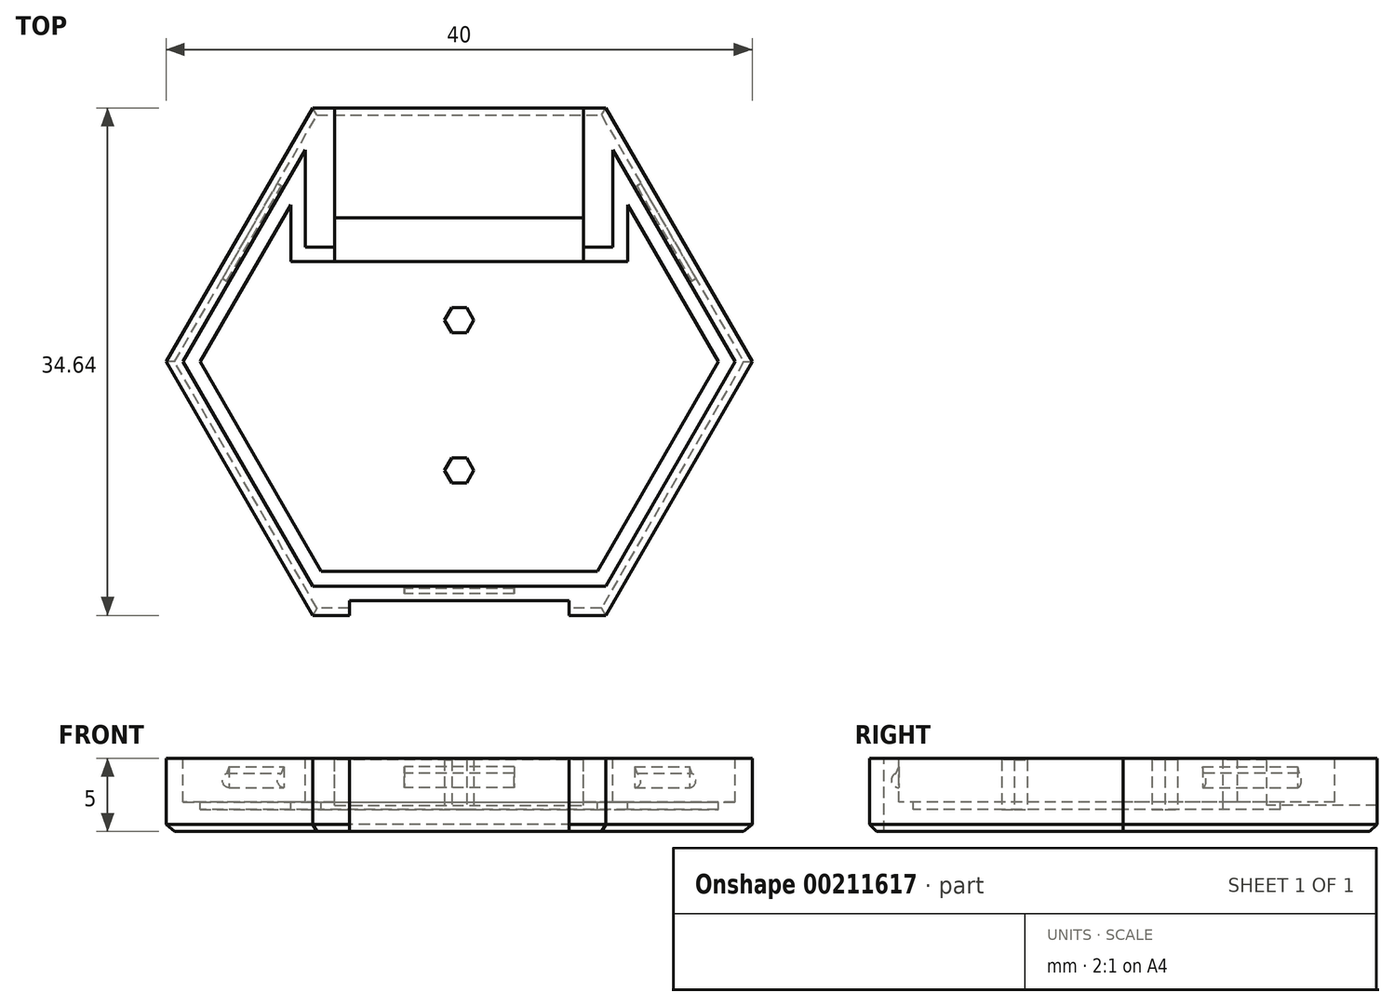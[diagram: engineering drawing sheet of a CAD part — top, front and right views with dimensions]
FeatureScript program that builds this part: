
annotation { "Feature Type Name" : "Feature", "Feature Type Description" : "" }
export const myFeature = defineFeature(function(context is Context, id is Id, definition is map)
    precondition{}
    {
        {
            var Q0;
            Q0=qCreatedBy(makeId("Top.planeOp"),FACE);
            var sketch = newSketch(context, id + "F0", { "sketchPlane" : qUnion([Q0])});
            skCircle(sketch, "E0.cCircle", {"center": v(0, 0) * mm, "radius": 20 * mm, "construction": true});
            skLineSegment(sketch, "E0.0", {"start": v(10, 17.32) * mm, "end": v(20, 0) * mm});
            skLineSegment(sketch, "E0.1", {"start": v(20, 0) * mm, "end": v(10, -17.32) * mm});
            skLineSegment(sketch, "E0.2", {"start": v(10, -17.32) * mm, "end": v(-10, -17.32) * mm});
            skLineSegment(sketch, "E0.3", {"start": v(-10, -17.32) * mm, "end": v(-20, 0) * mm});
            skLineSegment(sketch, "E0.4", {"start": v(-20, 0) * mm, "end": v(-10, 17.32) * mm});
            skLineSegment(sketch, "E0.5", {"start": v(-10, 17.32) * mm, "end": v(10, 17.32) * mm});
            skSolve(sketch);
        }
        {
            var Q0;
            Q0 = qSketchRegion(id + "F0", true);
            extrude(context, id + "F1", {"entities" : qUnion([Q0]), "depth" : 5 * mm});
        }
        {
            var Q0;
            Q0=makeQuery(id+"F1.opExtrude","SWEPT_FACE",FACE,{"disambiguationData":[OSD([sQuery(id+"F0.wireOp",EDGE,"E0.2")])]});
            var sketch = newSketch(context, id + "F2", { "sketchPlane" : qUnion([Q0])});
            skLineSegment(sketch, "E1.bottom", {"start": v(-7.5, 0) * mm, "end": v(7.5, 0) * mm});
            skLineSegment(sketch, "E1.top", {"start": v(-7.5, 5) * mm, "end": v(7.5, 5) * mm});
            skLineSegment(sketch, "E1.left", {"start": v(-7.5, 0) * mm, "end": v(-7.5, 5) * mm});
            skLineSegment(sketch, "E1.right", {"start": v(7.5, 0) * mm, "end": v(7.5, 5) * mm});
            skPoint(sketch, "E1.middle", {"position": v(0, 2.5) * mm});
            skLineSegment(sketch, "E2", {"start": v(-7.5, 5) * mm, "end": v(-7.5, 3.33) * mm});
            skLineSegment(sketch, "E3", {"start": v(-7.5, 3.33) * mm, "end": v(7.5, 3.33) * mm});
            skLineSegment(sketch, "E4", {"start": v(7.5, 3.33) * mm, "end": v(7.5, 1.67) * mm});
            skLineSegment(sketch, "E5", {"start": v(7.5, 1.67) * mm, "end": v(-7.5, 1.67) * mm});
            skLineSegment(sketch, "E6", {"start": v(-7.5, 1.67) * mm, "end": v(-7.5, 0) * mm});
            skLineSegment(sketch, "E7.left", {"start": v(-7.5, 5) * mm, "end": v(-7.5, 5) * mm});
            skLineSegment(sketch, "E7.right", {"start": v(7.5, 5) * mm, "end": v(7.5, 5) * mm});
            skSolve(sketch);
        }
        {
            var Q0;
            Q0=makeQuery(id+"F2.imprint","IMPRINT",FACE,{"disambiguationData":[TD([[makeQuery(id+"F2.imprint","IMPRINT",EDGE,{"derivedFrom":sQuery(id+"F2.wireOp",EDGE,"E1.left")}),-1.0]])]});
            var Q1;
            Q1=makeQuery(id+"F2.imprint","IMPRINT",FACE,{"disambiguationData":[TD([[makeQuery(id+"F2.imprint","IMPRINT",EDGE,{"derivedFrom":sQuery(id+"F2.wireOp",EDGE,"E1.top")}),1.0]])]});
            extrude(context, id + "F3", {"entities" : qUnion([Q0, Q1]), "operationType" : NewBodyOperationType.REMOVE, "oppositeDirection" : true, "depth" : 1 * mm});
        }
        {
            var Q0;
            Q0=makeQuery(id+"F1.opExtrude","CAP_FACE",FACE,{"disambiguationData":[OSD([sQuery(id+"F0.wireOp",EDGE,"E0.0"),sQuery(id+"F0.wireOp",EDGE,"E0.1"),sQuery(id+"F0.wireOp",EDGE,"E0.2"),sQuery(id+"F0.wireOp",EDGE,"E0.3"),sQuery(id+"F0.wireOp",EDGE,"E0.4"),sQuery(id+"F0.wireOp",EDGE,"E0.5")])],"isStart":false});
            var sketch = newSketch(context, id + "F4", { "sketchPlane" : qUnion([Q0])});
            skLineSegment(sketch, "E8.0", {"start": v(-18.85, 0) * mm, "end": v(-10, -15.32) * mm});
            skLineSegment(sketch, "E8.1", {"start": v(10, -15.32) * mm, "end": v(18.85, 0) * mm});
            skLineSegment(sketch, "E8.2", {"start": v(18.85, 0) * mm, "end": v(9.42, 16.32) * mm});
            skLineSegment(sketch, "E8.3", {"start": v(-10, -15.32) * mm, "end": v(10, -15.32) * mm});
            skLineSegment(sketch, "E8.4", {"start": v(9.42, 16.32) * mm, "end": v(-9.42, 16.32) * mm});
            skLineSegment(sketch, "E8.5", {"start": v(-9.42, 16.32) * mm, "end": v(-18.85, 0) * mm});
            skLineSegment(sketch, "E9.0", {"start": v(8.85, 15.32) * mm, "end": v(-8.85, 15.32) * mm});
            skLineSegment(sketch, "E9.1", {"start": v(-17.7, 0) * mm, "end": v(-9.42, -14.32) * mm});
            skLineSegment(sketch, "E9.2", {"start": v(-9.42, -14.32) * mm, "end": v(9.42, -14.32) * mm});
            skLineSegment(sketch, "E9.3", {"start": v(-8.85, 15.32) * mm, "end": v(-17.7, 0) * mm});
            skLineSegment(sketch, "E9.4", {"start": v(9.42, -14.32) * mm, "end": v(17.7, 0) * mm});
            skLineSegment(sketch, "E9.5", {"start": v(17.7, 0) * mm, "end": v(8.85, 15.32) * mm});
            skLineSegment(sketch, "E10.bottom", {"start": v(8.5, 17.32) * mm, "end": v(-8.5, 17.32) * mm});
            skLineSegment(sketch, "E10.top", {"start": v(8.5, 9.82) * mm, "end": v(-8.5, 9.82) * mm});
            skLineSegment(sketch, "E10.left", {"start": v(8.5, 17.32) * mm, "end": v(8.5, 9.82) * mm});
            skLineSegment(sketch, "E10.right", {"start": v(-8.5, 17.32) * mm, "end": v(-8.5, 9.82) * mm});
            skPoint(sketch, "E10.middle", {"position": v(0, 13.57) * mm});
            skLineSegment(sketch, "E11.0", {"start": v(10.5, 17.32) * mm, "end": v(10.5, 7.82) * mm});
            skLineSegment(sketch, "E11.1", {"start": v(10.5, 7.82) * mm, "end": v(-10.5, 7.82) * mm});
            skLineSegment(sketch, "E11.2", {"start": v(-10.5, 17.32) * mm, "end": v(-10.5, 7.82) * mm});
            skLineSegment(sketch, "E12.0", {"start": v(11.5, 17.32) * mm, "end": v(11.5, 6.82) * mm});
            skLineSegment(sketch, "E12.1", {"start": v(11.5, 6.82) * mm, "end": v(-11.5, 6.82) * mm});
            skLineSegment(sketch, "E12.2", {"start": v(-11.5, 17.32) * mm, "end": v(-11.5, 6.82) * mm});
            skPoint(sketch, "E13", {"position": v(-11.5, 10.72) * mm});
            skPoint(sketch, "E14", {"position": v(-11.5, 12.72) * mm});
            skPoint(sketch, "E15", {"position": v(-10.5, 14.45) * mm});
            skPoint(sketch, "E16", {"position": v(-10.5, 12.45) * mm});
            skPoint(sketch, "E17", {"position": v(10.5, 12.45) * mm});
            skPoint(sketch, "E18", {"position": v(11.5, 12.72) * mm});
            skPoint(sketch, "E19", {"position": v(10.5, 14.45) * mm});
            skPoint(sketch, "E20", {"position": v(11.5, 10.72) * mm});
            skLineSegment(sketch, "E21", {"start": v(-8.5, 9.82) * mm, "end": v(-8.5, 6.82) * mm});
            skLineSegment(sketch, "E22", {"start": v(8.5, 9.82) * mm, "end": v(8.5, 6.82) * mm});
            skSolve(sketch);
        }
        {
            var Q0;
            {var subQ5=sQuery(id+"F4.wireOp",EDGE,"E10.top");Q0=makeQuery(id+"F4.imprint","IMPRINT",FACE,{"disambiguationData":[TD([[makeQuery(id+"F4.imprint","IMPRINT",EDGE,{"derivedFrom":subQ5}),-1.0]])]});}
            var Q1;
            {var subQ0=sQuery(id+"F4.wireOp",EDGE,"E10.left");var subQ1=sQuery(id+"F4.wireOp",EDGE,"E8.4");var subQ2=makeQuery(id+"F4.imprint","INTERSECT",VERTEX,{"derivedFrom":[subQ1,subQ0]});Q1=makeQuery(id+"F4.imprint","IMPRINT",FACE,{"disambiguationData":[TD([[makeQuery(id+"F4.imprint","IMPRINT",EDGE,{"disambiguationData":[TD([[subQ2,-1.0]])],"derivedFrom":subQ1}),1.0]])]});}
            var Q2;
            {var subQ5=sQuery(id+"F4.wireOp",EDGE,"E10.bottom");Q2=makeQuery(id+"F4.imprint","IMPRINT",FACE,{"disambiguationData":[TD([[makeQuery(id+"F4.imprint","IMPRINT",EDGE,{"derivedFrom":subQ5}),-1.0]])]});}
            extrude(context, id + "F5", {"entities" : qUnion([Q0, Q1, Q2]), "operationType" : NewBodyOperationType.REMOVE, "oppositeDirection" : true, "depth" : 3.2 * mm});
        }
        {
            var Q0;
            {var subQ1=sQuery(id+"F4.wireOp",EDGE,"E9.1");Q0=makeQuery(id+"F4.imprint","IMPRINT",FACE,{"disambiguationData":[TD([[makeQuery(id+"F4.imprint","IMPRINT",EDGE,{"derivedFrom":subQ1}),1.0]])]});}
            extrude(context, id + "F6", {"entities" : qUnion([Q0]), "operationType" : NewBodyOperationType.REMOVE, "oppositeDirection" : true, "depth" : 3.5 * mm});
        }
        {
            var Q0;
            {var subQ0=sQuery(id+"F4.wireOp",EDGE,"E10.top");Q0=makeQuery(id+"F4.imprint","IMPRINT",FACE,{"disambiguationData":[TD([[makeQuery(id+"F4.imprint","IMPRINT",EDGE,{"derivedFrom":subQ0}),1.0]])]});}
            var Q1;
            {var subQ0=sQuery(id+"F4.wireOp",EDGE,"E22");var subQ1=sQuery(id+"F4.wireOp",EDGE,"E11.1");var subQ2=makeQuery(id+"F4.imprint","INTERSECT",VERTEX,{"derivedFrom":[subQ1,subQ0]});Q1=makeQuery(id+"F4.imprint","IMPRINT",FACE,{"disambiguationData":[TD([[makeQuery(id+"F4.imprint","IMPRINT",EDGE,{"disambiguationData":[TD([[subQ2,-1.0]])],"derivedFrom":subQ1}),1.0]])]});}
            extrude(context, id + "F7", {"entities" : qUnion([Q0, Q1]), "operationType" : NewBodyOperationType.REMOVE, "oppositeDirection" : true, "depth" : 0.1 * mm});
        }
        {
            var Q0;
            {var subQ5=sQuery(id+"F4.wireOp",EDGE,"E11.2");var subQ8=sQuery(id+"F4.wireOp",EDGE,"E9.3");var subQ9=makeQuery(id+"F4.imprint","INTERSECT",VERTEX,{"derivedFrom":[subQ8,subQ5]});Q0=makeQuery(id+"F4.imprint","IMPRINT",FACE,{"disambiguationData":[TD([[makeQuery(id+"F4.imprint","IMPRINT",EDGE,{"disambiguationData":[TD([[subQ9,-1.0]])],"derivedFrom":subQ8}),1.0]])]});}
            var Q1;
            {var subQ0=sQuery(id+"F4.wireOp",EDGE,"E11.2");var subQ1=sQuery(id+"F4.wireOp",EDGE,"E8.5");var subQ2=makeQuery(id+"F4.imprint","INTERSECT",VERTEX,{"derivedFrom":[subQ1,subQ0]});Q1=makeQuery(id+"F4.imprint","IMPRINT",FACE,{"disambiguationData":[TD([[makeQuery(id+"F4.imprint","IMPRINT",EDGE,{"disambiguationData":[TD([[subQ2,-1.0]])],"derivedFrom":subQ1}),1.0]])]});}
            var Q2;
            {var subQ5=sQuery(id+"F4.wireOp",EDGE,"E8.0");Q2=makeQuery(id+"F4.imprint","IMPRINT",FACE,{"disambiguationData":[TD([[makeQuery(id+"F4.imprint","IMPRINT",EDGE,{"derivedFrom":subQ5}),1.0]])]});}
            var Q3;
            {var subQ1=sQuery(id+"F4.wireOp",EDGE,"E12.0");var subQ3=sQuery(id+"F4.wireOp",EDGE,"E9.5");var subQ4=makeQuery(id+"F4.imprint","INTERSECT",VERTEX,{"derivedFrom":[subQ3,subQ1]});Q3=makeQuery(id+"F4.imprint","IMPRINT",FACE,{"disambiguationData":[TD([[makeQuery(id+"F4.imprint","IMPRINT",EDGE,{"disambiguationData":[TD([[subQ4,-1.0]])],"derivedFrom":subQ3}),1.0]])]});}
            var Q4;
            {var subQ0=sQuery(id+"F4.wireOp",EDGE,"E12.0");var subQ1=sQuery(id+"F4.wireOp",EDGE,"E8.2");var subQ2=makeQuery(id+"F4.imprint","INTERSECT",VERTEX,{"derivedFrom":[subQ1,subQ0]});Q4=makeQuery(id+"F4.imprint","IMPRINT",FACE,{"disambiguationData":[TD([[makeQuery(id+"F4.imprint","IMPRINT",EDGE,{"disambiguationData":[TD([[subQ2,-1.0]])],"derivedFrom":subQ1}),1.0]])]});}
            extrude(context, id + "F8", {"entities" : qUnion([Q0, Q1, Q2, Q3, Q4]), "operationType" : NewBodyOperationType.REMOVE, "oppositeDirection" : true, "depth" : 3 * mm});
        }
        {
            var Q0;
            Q0=makeQuery(id+"F6.boolean.opBoolean","COPY",FACE,{"derivedFrom":makeQuery(id+"F6.opExtrude","CAP_FACE",FACE,{"disambiguationData":[OSD([sQuery(id+"F4.wireOp",EDGE,"E9.1"),sQuery(id+"F4.wireOp",EDGE,"E9.2"),sQuery(id+"F4.wireOp",EDGE,"E9.3"),sQuery(id+"F4.wireOp",EDGE,"E9.4"),sQuery(id+"F4.wireOp",EDGE,"E9.5"),sQuery(id+"F4.wireOp",EDGE,"E12.0"),sQuery(id+"F4.wireOp",EDGE,"E12.1"),sQuery(id+"F4.wireOp",EDGE,"E12.2")])],"isStart":false})});
            var sketch = newSketch(context, id + "F9", { "sketchPlane" : qUnion([Q0])});
            skCircle(sketch, "E23.cCircle", {"center": v(0, 2.84) * mm, "radius": 1 * mm, "construction": true});
            skLineSegment(sketch, "E23.0", {"start": v(0.5, 1.97) * mm, "end": v(-0.5, 1.97) * mm});
            skLineSegment(sketch, "E23.1", {"start": v(-0.5, 1.97) * mm, "end": v(-1, 2.84) * mm});
            skLineSegment(sketch, "E23.2", {"start": v(-1, 2.84) * mm, "end": v(-0.5, 3.7) * mm});
            skLineSegment(sketch, "E23.3", {"start": v(-0.5, 3.7) * mm, "end": v(0.5, 3.7) * mm});
            skLineSegment(sketch, "E23.4", {"start": v(0.5, 3.7) * mm, "end": v(1, 2.84) * mm});
            skLineSegment(sketch, "E23.5", {"start": v(1, 2.84) * mm, "end": v(0.5, 1.97) * mm});
            skLineSegment(sketch, "E24", {"start": v(-6.8, -2.3) * mm, "end": v(7.3, -2.3) * mm});
            skLineSegment(sketch, "E25.MirrorCS", {"start": v(0.5, -6.56) * mm, "end": v(-0.5, -6.56) * mm});
            skLineSegment(sketch, "E26.MirrorCS", {"start": v(-0.5, -6.56) * mm, "end": v(-1, -7.43) * mm});
            skLineSegment(sketch, "E27.MirrorCS", {"start": v(-1, -7.43) * mm, "end": v(-0.5, -8.3) * mm});
            skLineSegment(sketch, "E28.MirrorCS", {"start": v(-0.5, -8.3) * mm, "end": v(0.5, -8.3) * mm});
            skLineSegment(sketch, "E29.MirrorCS", {"start": v(0.5, -8.3) * mm, "end": v(1, -7.43) * mm});
            skCircle(sketch, "E30.MirrorC", {"center": v(0, -7.43) * mm, "radius": 1 * mm, "construction": true});
            skLineSegment(sketch, "E31.MirrorCS", {"start": v(1, -7.43) * mm, "end": v(0.5, -6.56) * mm});
            skSolve(sketch);
        }
        {
            var Q0;
            Q0=makeQuery(id+"F9.imprint","IMPRINT",FACE,{"disambiguationData":[TD([[makeQuery(id+"F9.imprint","IMPRINT",EDGE,{"derivedFrom":sQuery(id+"F9.wireOp",EDGE,"E23.0")}),-1.0]])]});
            var Q1;
            Q1=makeQuery(id+"F9.imprint","IMPRINT",FACE,{"disambiguationData":[TD([[makeQuery(id+"F9.imprint","IMPRINT",EDGE,{"derivedFrom":sQuery(id+"F9.wireOp",EDGE,"E25.MirrorCS")}),1.0]])]});
            extrude(context, id + "F10", {"entities" : qUnion([Q0, Q1]), "operationType" : NewBodyOperationType.ADD, "depth" : 3.4 * mm});
        }
        {
            var Q0;
            Q0=makeQuery(id+"F8.boolean.opBoolean","COPY",FACE,{"derivedFrom":makeQuery(id+"F8.opExtrude","SWEPT_FACE",FACE,{"disambiguationData":[OSD([sQuery(id+"F4.wireOp",EDGE,"E8.3")])]})});
            var sketch = newSketch(context, id + "F11", { "sketchPlane" : qUnion([Q0])});
            skLineSegment(sketch, "E32.bottom", {"start": v(3.75, 4) * mm, "end": v(-3.75, 4) * mm});
            skLineSegment(sketch, "E32.top", {"start": v(3.75, 3) * mm, "end": v(-3.75, 3) * mm});
            skLineSegment(sketch, "E32.left", {"start": v(3.75, 4) * mm, "end": v(3.75, 3) * mm});
            skLineSegment(sketch, "E32.right", {"start": v(-3.75, 4) * mm, "end": v(-3.75, 3) * mm});
            skPoint(sketch, "E32.middle", {"position": v(0, 3.5) * mm});
            skLineSegment(sketch, "E33", {"start": v(-3.75, 3.5) * mm, "end": v(3.75, 3.5) * mm});
            skSolve(sketch);
        }
        {
            var Q0;
            Q0=makeQuery(id+"F8.boolean.opBoolean","COPY",FACE,{"derivedFrom":makeQuery(id+"F8.opExtrude","SWEPT_FACE",FACE,{"disambiguationData":[OSD([sQuery(id+"F4.wireOp",EDGE,"E8.2")])]})});
            var sketch = newSketch(context, id + "F12", { "sketchPlane" : qUnion([Q0])});
            skLineSegment(sketch, "E34.bottom", {"start": v(3.17, 4) * mm, "end": v(-4.33, 4) * mm});
            skLineSegment(sketch, "E34.top", {"start": v(3.17, 3) * mm, "end": v(-4.33, 3) * mm});
            skLineSegment(sketch, "E34.left", {"start": v(3.17, 4) * mm, "end": v(3.17, 3) * mm});
            skLineSegment(sketch, "E34.right", {"start": v(-4.33, 4) * mm, "end": v(-4.33, 3) * mm});
            skPoint(sketch, "E34.middle", {"position": v(-0.58, 3.5) * mm});
            skLineSegment(sketch, "E35", {"start": v(-4.33, 3.5) * mm, "end": v(3.17, 3.5) * mm});
            skSolve(sketch);
        }
        {
            var Q0;
            Q0=makeQuery(id+"F8.boolean.opBoolean","COPY",FACE,{"derivedFrom":makeQuery(id+"F8.opExtrude","SWEPT_FACE",FACE,{"disambiguationData":[OSD([sQuery(id+"F4.wireOp",EDGE,"E8.5")])]})});
            var sketch = newSketch(context, id + "F13", { "sketchPlane" : qUnion([Q0])});
            skLineSegment(sketch, "E36.bottom", {"start": v(4.33, 4) * mm, "end": v(-3.17, 4) * mm});
            skLineSegment(sketch, "E36.top", {"start": v(4.33, 3) * mm, "end": v(-3.17, 3) * mm});
            skLineSegment(sketch, "E36.left", {"start": v(4.33, 4) * mm, "end": v(4.33, 3) * mm});
            skLineSegment(sketch, "E36.right", {"start": v(-3.17, 4) * mm, "end": v(-3.17, 3) * mm});
            skPoint(sketch, "E36.middle", {"position": v(0.58, 3.5) * mm});
            skLineSegment(sketch, "E37", {"start": v(-3.17, 3.5) * mm, "end": v(4.33, 3.5) * mm});
            skSolve(sketch);
        }
        {
            var Q0;
            {var subQ0=sQuery(id+"F11.wireOp",EDGE,"E32.top");Q0=makeQuery(id+"F11.imprint","IMPRINT",FACE,{"disambiguationData":[TD([[makeQuery(id+"F11.imprint","IMPRINT",EDGE,{"derivedFrom":subQ0}),-1.0]])]});}
            var Q1;
            Q1=sQuery(id+"F11.wireOp",EDGE,"E33");
            revolve(context, id + "F14", {"operationType" : NewBodyOperationType.REMOVE, "entities" : qUnion([Q0]), "axis" : qUnion([Q1]), "revolveType" : RevolveType.FULL, "oppositeDirection" : true});
        }
        {
            var Q0;
            {var subQ0=sQuery(id+"F12.wireOp",EDGE,"E34.top");Q0=makeQuery(id+"F12.imprint","IMPRINT",FACE,{"disambiguationData":[TD([[makeQuery(id+"F12.imprint","IMPRINT",EDGE,{"derivedFrom":subQ0}),-1.0]])]});}
            var Q1;
            Q1=sQuery(id+"F12.wireOp",EDGE,"E35");
            revolve(context, id + "F15", {"operationType" : NewBodyOperationType.REMOVE, "entities" : qUnion([Q0]), "axis" : qUnion([Q1]), "revolveType" : RevolveType.FULL, "oppositeDirection" : true});
        }
        {
            var Q0;
            {var subQ0=sQuery(id+"F13.wireOp",EDGE,"E36.top");Q0=makeQuery(id+"F13.imprint","IMPRINT",FACE,{"disambiguationData":[TD([[makeQuery(id+"F13.imprint","IMPRINT",EDGE,{"derivedFrom":subQ0}),-1.0]])]});}
            var Q1;
            Q1=sQuery(id+"F13.wireOp",EDGE,"E37");
            revolve(context, id + "F16", {"operationType" : NewBodyOperationType.REMOVE, "entities" : qUnion([Q0]), "axis" : qUnion([Q1]), "revolveType" : RevolveType.FULL, "oppositeDirection" : true});
        }
        {
            var Q0;
            Q0=makeQuery(id+"F1.opExtrude","CAP_EDGE",EDGE,{"disambiguationData":[OSD([sQuery(id+"F0.wireOp",EDGE,"E0.0")])],"isStart":true});
            var Q1;
            Q1=makeQuery(id+"F1.opExtrude","CAP_EDGE",EDGE,{"disambiguationData":[OSD([sQuery(id+"F0.wireOp",EDGE,"E0.1")])],"isStart":true});
            var Q2;
            Q2=makeQuery(id+"F1.opExtrude","CAP_EDGE",EDGE,{"disambiguationData":[OSD([sQuery(id+"F0.wireOp",EDGE,"E0.5")])],"isStart":true});
            var Q3;
            Q3=makeQuery(id+"F1.opExtrude","CAP_EDGE",EDGE,{"disambiguationData":[OSD([sQuery(id+"F0.wireOp",EDGE,"E0.4")])],"isStart":true});
            var Q4;
            Q4=makeQuery(id+"F1.opExtrude","CAP_EDGE",EDGE,{"disambiguationData":[OSD([sQuery(id+"F0.wireOp",EDGE,"E0.3")])],"isStart":true});
            var Q5;
            Q5=makeQuery(id+"F1.opExtrude","CAP_EDGE",EDGE,{"disambiguationData":[OSD([sQuery(id+"F0.wireOp",EDGE,"E0.2")])],"isStart":true});
            var Q6;
            Q6=makeQuery(id+"F5.boolean.opBoolean","COPY",EDGE,{"derivedFrom":makeQuery(id+"F5.opExtrude","CAP_EDGE",EDGE,{"disambiguationData":[OSD([sQuery(id+"F4.wireOp",EDGE,"E10.bottom")])],"isStart":false})});
            var Q7;
            Q7=makeQuery(id+"F5.boolean.opBoolean","COPY",EDGE,{"derivedFrom":makeQuery(id+"F5.opExtrude","SWEPT_EDGE",EDGE,{"disambiguationData":[OSD([sQuery(id+"F0.wireOp",EDGE,"E0.5"),sQuery(id+"F4.wireOp",EDGE,"E10.bottom"),sQuery(id+"F4.wireOp",EDGE,"E10.right")])]})});
            var Q8;
            Q8=makeQuery(id+"F5.boolean.opBoolean","COPY",EDGE,{"derivedFrom":makeQuery(id+"F5.opExtrude","SWEPT_EDGE",EDGE,{"disambiguationData":[OSD([sQuery(id+"F0.wireOp",EDGE,"E0.5"),sQuery(id+"F4.wireOp",EDGE,"E10.bottom"),sQuery(id+"F4.wireOp",EDGE,"E10.left")])]})});
            chamfer(context, id + "F17", {"entities" : qUnion([Q0, Q1, Q2, Q3, Q4, Q5, Q6, Q7, Q8]), "width" : 0.5 * mm, "tangentPropagation" : true});
        }
        {
            var Q0;
            Q0=makeQuery(id+"F15.boolean.opBoolean","INTERSECT",EDGE,{"disambiguationData":[OD(1.0)],"derivedFrom":[makeQuery(id+"F8.boolean.opBoolean","COPY",FACE,{"derivedFrom":makeQuery(id+"F8.opExtrude","SWEPT_FACE",FACE,{"disambiguationData":[OSD([sQuery(id+"F4.wireOp",EDGE,"E8.2")])]})}),makeQuery(id+"F15.opRevolve","SWEPT_FACE",FACE,{"disambiguationData":[OSD([sQuery(id+"F12.wireOp",EDGE,"E34.top")])]})]});
            var Q1;
            Q1=makeQuery(id+"F16.boolean.opBoolean","INTERSECT",EDGE,{"disambiguationData":[OD(1.0)],"derivedFrom":[makeQuery(id+"F8.boolean.opBoolean","COPY",FACE,{"derivedFrom":makeQuery(id+"F8.opExtrude","SWEPT_FACE",FACE,{"disambiguationData":[OSD([sQuery(id+"F4.wireOp",EDGE,"E8.5")])]})}),makeQuery(id+"F16.opRevolve","SWEPT_FACE",FACE,{"disambiguationData":[OSD([sQuery(id+"F13.wireOp",EDGE,"E36.top")])]})]});
            var Q2;
            Q2=makeQuery(id+"F14.boolean.opBoolean","INTERSECT",EDGE,{"disambiguationData":[OD(1.0)],"derivedFrom":[makeQuery(id+"F8.boolean.opBoolean","COPY",FACE,{"derivedFrom":makeQuery(id+"F8.opExtrude","SWEPT_FACE",FACE,{"disambiguationData":[OSD([sQuery(id+"F4.wireOp",EDGE,"E8.3")])]})}),makeQuery(id+"F14.opRevolve","SWEPT_FACE",FACE,{"disambiguationData":[OSD([sQuery(id+"F11.wireOp",EDGE,"E32.top")])]})]});
            chamfer(context, id + "F18", {"entities" : qUnion([Q0, Q1, Q2]), "chamferType" : ChamferType.OFFSET_ANGLE, "width" : 0.5 * mm, "oppositeDirection" : false, "angle" : 35 * degree, "tangentPropagation" : true});
        }
    });
